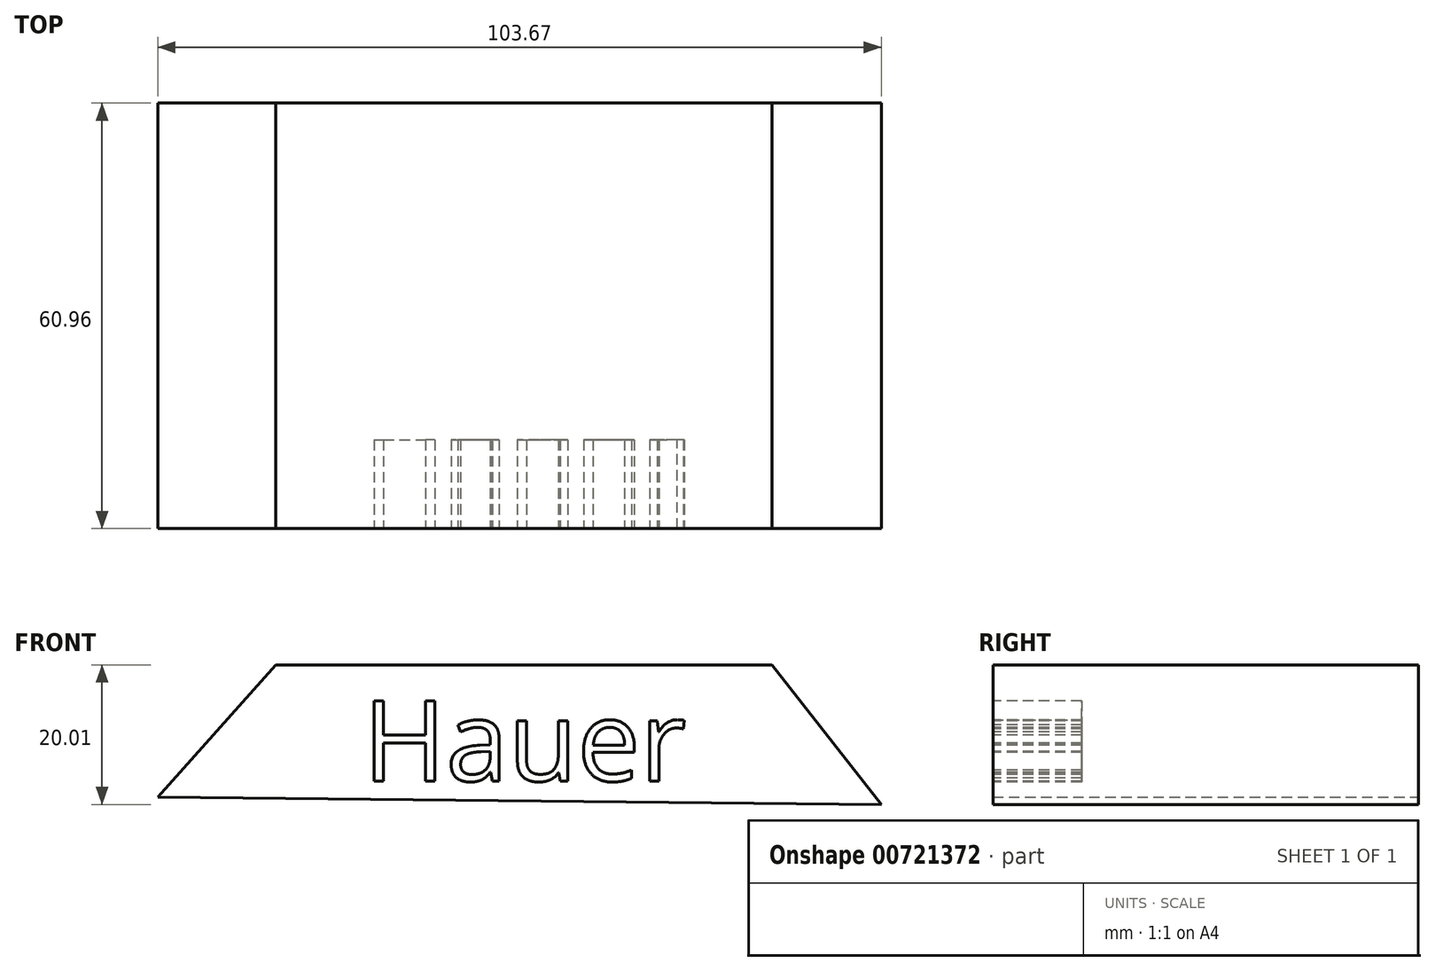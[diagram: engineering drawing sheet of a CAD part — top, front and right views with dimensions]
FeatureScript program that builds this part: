
annotation { "Feature Type Name" : "Feature", "Feature Type Description" : "" }
export const myFeature = defineFeature(function(context is Context, id is Id, definition is map)
    precondition{}
    {
        {
            var Q0;
            Q0=qCreatedBy(makeId("Front.planeOp"),FACE);
            var sketch = newSketch(context, id + "F0", { "sketchPlane" : qUnion([Q0])});
            skLineSegment(sketch, "E0", {"start": v(0, 0) * mm, "end": v(35.56, 0) * mm});
            skLineSegment(sketch, "E1", {"start": v(35.56, 0) * mm, "end": v(51.2, -20.01) * mm});
            skLineSegment(sketch, "E2", {"start": v(0, 0) * mm, "end": v(-35.56, 0) * mm});
            skLineSegment(sketch, "E3", {"start": v(-35.56, 0) * mm, "end": v(-52.47, -18.95) * mm});
            skLineSegment(sketch, "E4", {"start": v(-52.47, -18.95) * mm, "end": v(51.2, -20.01) * mm});
            skSolve(sketch);
        }
        {
            var Q0;
            Q0 = qSketchRegion(id + "F0", true);
            extrude(context, id + "F1", {"entities" : qUnion([Q0]), "depth" : 60.96 * mm, "offsetDistance" : 25.4 * mm});
        }
        {
            var Q0;
            Q0=makeQuery(id+"F1.opExtrude","CAP_FACE",FACE,{"disambiguationData":[OSD([sQuery(id+"F0.wireOp",EDGE,"E0"),sQuery(id+"F0.wireOp",EDGE,"E1"),sQuery(id+"F0.wireOp",EDGE,"E2"),sQuery(id+"F0.wireOp",EDGE,"E3"),sQuery(id+"F0.wireOp",EDGE,"E4")])],"isStart":false});
            var sketch = newSketch(context, id + "F2", { "sketchPlane" : qUnion([Q0])});
            skText(sketch, "E5", { "text": "Hauer", "fontName": "OpenSans-Regular.ttf"});
            const initialGuessF2  = {"E5": [-0.02305, -0.01664, 1, 0, 0.01158]};
            skSetInitialGuess(sketch, initialGuessF2);
            skSolve(sketch);
        }
        {
            var Q0;
            Q0 = qSketchRegion(id + "F2", true);
            extrude(context, id + "F3", {"entities" : qUnion([Q0]), "operationType" : NewBodyOperationType.REMOVE, "oppositeDirection" : true, "depth" : 12.7 * mm, "offsetDistance" : 25.4 * mm});
        }
    });
